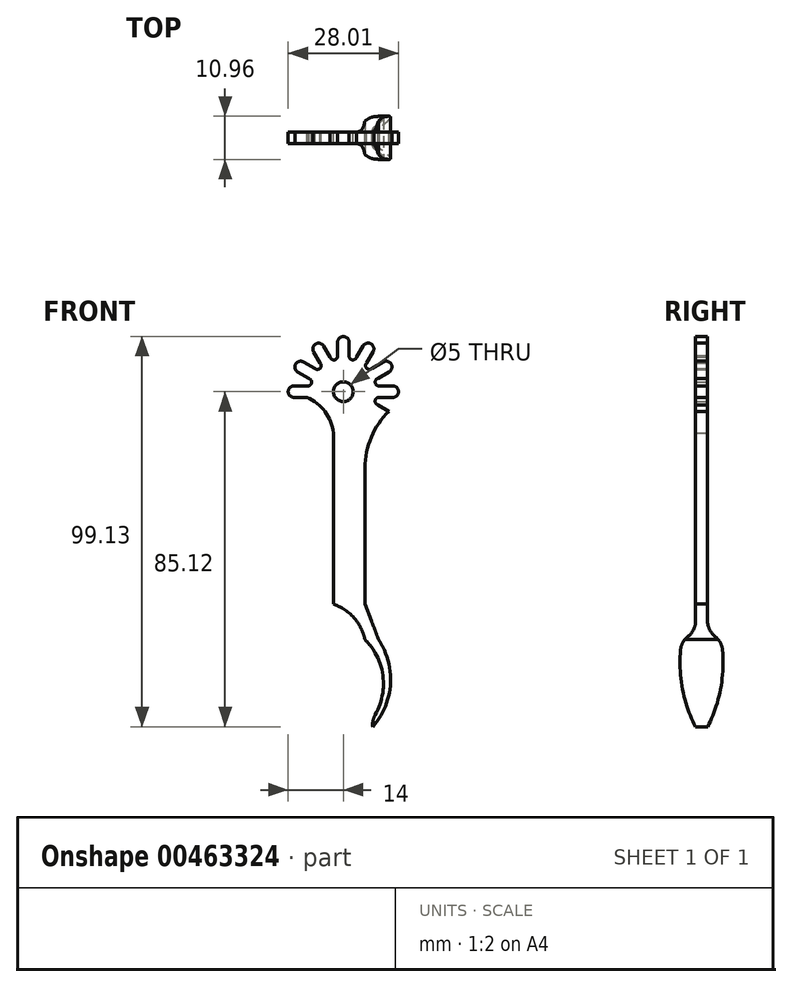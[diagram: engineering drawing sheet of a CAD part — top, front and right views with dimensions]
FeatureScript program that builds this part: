
annotation { "Feature Type Name" : "Feature", "Feature Type Description" : "" }
export const myFeature = defineFeature(function(context is Context, id is Id, definition is map)
    precondition{}
    {
        {
            var Q0;
            Q0=qCreatedBy(makeId("Front.planeOp"),FACE);
            var sketch = newSketch(context, id + "F0", { "sketchPlane" : qUnion([Q0])});
            skCircle(sketch, "E0", {"center": v(0, 0) * mm, "radius": 14 * mm, "construction": true});
            skCircle(sketch, "E1", {"center": v(0, 0) * mm, "radius": 2.5 * mm});
            skLineSegment(sketch, "E2", {"start": v(-12.53, 1.48) * mm, "end": v(-9.23, 1.48) * mm});
            skArc(sketch, "E3", {"start": v(-12.53, 1.48) * mm, "mid": v(-14, 0) * mm, "end": v(-12.53, -1.48) * mm});
            skLineSegment(sketch, "E4", {"start": v(-12.53, -1.48) * mm, "end": v(-9.23, -1.48) * mm});
            skPoint(sketch, "E5.center", {"position": v(-0.01, 0.04) * mm});
            skLineSegment(sketch, "E6.1.0", {"start": v(-11.58, 4.99) * mm, "end": v(-8.73, 3.34) * mm});
            skArc(sketch, "E6.1.1", {"start": v(-10.1, 7.54) * mm, "mid": v(-12.12, 7) * mm, "end": v(-11.58, 4.99) * mm});
            skLineSegment(sketch, "E6.1.2", {"start": v(-10.1, 7.54) * mm, "end": v(-7.26, 5.9) * mm});
            skLineSegment(sketch, "E6.2.0", {"start": v(-7.54, 10.11) * mm, "end": v(-5.9, 7.27) * mm});
            skArc(sketch, "E6.2.1", {"start": v(-4.98, 11.59) * mm, "mid": v(-7, 12.13) * mm, "end": v(-7.54, 10.11) * mm});
            skLineSegment(sketch, "E6.2.2", {"start": v(-4.98, 11.59) * mm, "end": v(-3.34, 8.74) * mm});
            skLineSegment(sketch, "E6.3.0", {"start": v(-1.47, 12.53) * mm, "end": v(-1.47, 9.24) * mm});
            skArc(sketch, "E6.3.1", {"start": v(1.48, 12.53) * mm, "mid": v(0, 14) * mm, "end": v(-1.47, 12.53) * mm});
            skLineSegment(sketch, "E6.3.2", {"start": v(1.48, 12.53) * mm, "end": v(1.48, 9.24) * mm});
            skLineSegment(sketch, "E6.4.0", {"start": v(5, 11.59) * mm, "end": v(3.35, 8.74) * mm});
            skArc(sketch, "E6.4.1", {"start": v(7.55, 10.11) * mm, "mid": v(7.01, 12.13) * mm, "end": v(5, 11.59) * mm});
            skLineSegment(sketch, "E6.4.2", {"start": v(7.55, 10.11) * mm, "end": v(5.9, 7.26) * mm});
            skLineSegment(sketch, "E6.5.0", {"start": v(10.12, 7.54) * mm, "end": v(7.27, 5.9) * mm});
            skArc(sketch, "E6.5.1", {"start": v(11.6, 4.99) * mm, "mid": v(12.14, 7) * mm, "end": v(10.12, 7.54) * mm});
            skLineSegment(sketch, "E6.5.2", {"start": v(11.6, 4.99) * mm, "end": v(8.75, 3.34) * mm});
            skLineSegment(sketch, "E6.6.0", {"start": v(12.54, 1.47) * mm, "end": v(9.25, 1.47) * mm});
            skArc(sketch, "E6.6.1", {"start": v(12.54, -1.48) * mm, "mid": v(14.01, 0) * mm, "end": v(12.54, 1.47) * mm});
            skLineSegment(sketch, "E6.6.2", {"start": v(12.54, -1.48) * mm, "end": v(9.25, -1.48) * mm});
            skLineSegment(sketch, "E6.7.0", {"start": v(11.6, -5) * mm, "end": v(8.75, -3.35) * mm});
            skLineSegment(sketch, "E6.anchor1", {"start": v(0, 0) * mm, "end": v(-12.53, -1.48) * mm, "construction": true});
            skLineSegment(sketch, "E6.anchor2", {"start": v(0, 0) * mm, "end": v(11.6, -5) * mm, "construction": true});
            skCircle(sketch, "E7", {"center": v(-0.01, 0.04) * mm, "radius": 9.33 * mm, "construction": true});
            skArc(sketch, "E8", {"start": v(-9.23, 1.47) * mm, "mid": v(-8.1, 2.17) * mm, "end": v(-8.73, 3.34) * mm});
            skArc(sketch, "E9.1.0", {"start": v(-7.26, 5.9) * mm, "mid": v(-5.92, 5.93) * mm, "end": v(-5.9, 7.27) * mm});
            skArc(sketch, "E9.2.0", {"start": v(-3.34, 8.74) * mm, "mid": v(-2.16, 8.1) * mm, "end": v(-1.47, 9.24) * mm});
            skArc(sketch, "E9.3.0", {"start": v(1.48, 9.24) * mm, "mid": v(2.18, 8.1) * mm, "end": v(3.35, 8.74) * mm});
            skArc(sketch, "E9.4.0", {"start": v(5.9, 7.26) * mm, "mid": v(5.94, 5.93) * mm, "end": v(7.27, 5.9) * mm});
            skArc(sketch, "E9.5.0", {"start": v(8.75, 3.34) * mm, "mid": v(8.1, 2.17) * mm, "end": v(9.25, 1.47) * mm});
            skArc(sketch, "E9.6.0", {"start": v(9.25, -1.48) * mm, "mid": v(8.1, -2.17) * mm, "end": v(8.75, -3.35) * mm});
            skLineSegment(sketch, "E9.anchor1", {"start": v(0, 0) * mm, "end": v(-9.24, 1.48) * mm, "construction": true});
            skLineSegment(sketch, "E9.anchor2", {"start": v(0, 0) * mm, "end": v(7.27, -5.9) * mm, "construction": true});
            skLineSegment(sketch, "E10", {"start": v(-2.48, -0.3) * mm, "end": v(-2.48, -38.57) * mm, "construction": true});
            skArc(sketch, "E11", {"start": v(-2.48, -10.54) * mm, "mid": v(-4.63, -5.1) * mm, "end": v(-9.23, -1.48) * mm});
            skLineSegment(sketch, "E12", {"start": v(-2.48, -10.54) * mm, "end": v(-2.48, -54) * mm});
            skLineSegment(sketch, "E13", {"start": v(-2.48, -54) * mm, "end": v(5.52, -54) * mm});
            skLineSegment(sketch, "E14", {"start": v(5.52, -54) * mm, "end": v(5.52, -19.35) * mm});
            skArc(sketch, "E15", {"start": v(11.6, -5) * mm, "mid": v(7.1, -11.55) * mm, "end": v(5.52, -19.35) * mm});
            skSolve(sketch);
        }
        {
            var Q0;
            Q0 = qSketchRegion(id + "F0", true);
            extrude(context, id + "F1", {"entities" : qUnion([Q0]), "endBound" : BoundingType.SYMMETRIC, "depth" : 3 * mm});
        }
        {
            var Q0;
            Q0=qCreatedBy(makeId("Front.planeOp"),FACE);
            var sketch = newSketch(context, id + "F2", { "sketchPlane" : qUnion([Q0])});
            skLineSegment(sketch, "E16.bottom", {"start": v(-9.48, -54) * mm, "end": v(12.52, -54) * mm});
            skLineSegment(sketch, "E16.top", {"start": v(-9.48, -87) * mm, "end": v(12.52, -87) * mm});
            skLineSegment(sketch, "E16.left", {"start": v(-9.48, -54) * mm, "end": v(-9.48, -87) * mm});
            skLineSegment(sketch, "E16.right", {"start": v(12.52, -54) * mm, "end": v(12.52, -87) * mm});
            skSolve(sketch);
        }
        {
            var Q0;
            Q0=makeQuery(id+"F2.imprint","IMPRINT",FACE,{"disambiguationData":[TD([[makeQuery(id+"F2.imprint","IMPRINT",EDGE,{"derivedFrom":sQuery(id+"F2.wireOp",EDGE,"E16.bottom")}),-1.0]])]});
            extrude(context, id + "F3", {"entities" : qUnion([Q0]), "operationType" : NewBodyOperationType.ADD, "endBound" : BoundingType.SYMMETRIC, "depth" : 25 * mm});
        }
        {
            var Q0;
            Q0=makeQuery(id+"F3.opExtrude","SWEPT_FACE",FACE,{"disambiguationData":[OSD([sQuery(id+"F2.wireOp",EDGE,"E16.right")])]});
            var sketch = newSketch(context, id + "F4", { "sketchPlane" : qUnion([Q0])});
            skLineSegment(sketch, "E17.bottom", {"start": v(-1.5, -54) * mm, "end": v(1.5, -54) * mm});
            skLineSegment(sketch, "E17.top", {"start": v(-1.5, -63) * mm, "end": v(1.5, -63) * mm});
            skLineSegment(sketch, "E17.left", {"start": v(-1.5, -54) * mm, "end": v(-1.5, -63) * mm});
            skLineSegment(sketch, "E17.right", {"start": v(1.5, -54) * mm, "end": v(1.5, -63) * mm});
            skLineSegment(sketch, "E18", {"start": v(5, -63) * mm, "end": v(-5, -63) * mm});
            skLineSegment(sketch, "E19", {"start": v(0, -63) * mm, "end": v(0, 139.5) * mm, "construction": true});
            skPoint(sketch, "E19.endSnap0", {"position": v(0, -87) * mm});
            skLineSegment(sketch, "E20", {"start": v(0, -87) * mm, "end": v(0, 118) * mm, "construction": true});
            skArc(sketch, "E21", {"start": v(0.54, -87) * mm, "mid": v(4.87, -75.4) * mm, "end": v(5, -63) * mm});
            skArc(sketch, "E22.MirrorCS", {"start": v(-0.54, -87) * mm, "mid": v(-4.87, -75.4) * mm, "end": v(-5, -63) * mm});
            skLineSegment(sketch, "E23", {"start": v(0.54, -87) * mm, "end": v(-0.54, -87) * mm});
            skSolve(sketch);
        }
        {
            var Q0;
            {var subQ4=sQuery(id+"F4.wireOp",EDGE,"E17.left");Q0=makeQuery(id+"F4.imprint","IMPRINT",FACE,{"disambiguationData":[TD([[makeQuery(id+"F4.imprint","IMPRINT",EDGE,{"derivedFrom":subQ4}),-1.0]])]});}
            var Q1;
            {var subQ4=sQuery(id+"F4.wireOp",EDGE,"E17.right");Q1=makeQuery(id+"F4.imprint","IMPRINT",FACE,{"disambiguationData":[TD([[makeQuery(id+"F4.imprint","IMPRINT",EDGE,{"derivedFrom":subQ4}),1.0]])]});}
            extrude(context, id + "F5", {"entities" : qUnion([Q0, Q1]), "operationType" : NewBodyOperationType.REMOVE, "oppositeDirection" : true, "depth" : 25 * mm});
        }
        {
            var Q0;
            Q0=qCreatedBy(makeId("Front.planeOp"),FACE);
            var sketch = newSketch(context, id + "F6", { "sketchPlane" : qUnion([Q0])});
            skLineSegment(sketch, "E24", {"start": v(5.52, -54) * mm, "end": v(8.93, -63) * mm});
            skLineSegment(sketch, "E25", {"start": v(8.93, -63) * mm, "end": v(19.75, -63) * mm});
            skLineSegment(sketch, "E26", {"start": v(19.75, -63) * mm, "end": v(18.1, -40.93) * mm});
            skLineSegment(sketch, "E27", {"start": v(18.1, -40.93) * mm, "end": v(5.52, -54) * mm});
            skSolve(sketch);
        }
        {
            var Q0;
            Q0 = qSketchRegion(id + "F6", true);
            extrude(context, id + "F7", {"entities" : qUnion([Q0]), "operationType" : NewBodyOperationType.REMOVE, "endBound" : BoundingType.SYMMETRIC, "depth" : 25 * mm});
        }
        {
            var Q0;
            Q0=qCreatedBy(makeId("Front.planeOp"),FACE);
            var sketch = newSketch(context, id + "F8", { "sketchPlane" : qUnion([Q0])});
            skLineSegment(sketch, "E28.bottom", {"start": v(-2.48, -54) * mm, "end": v(-15.55, -54) * mm});
            skLineSegment(sketch, "E28.top", {"start": v(-2.48, -90.5) * mm, "end": v(-15.55, -90.5) * mm});
            skLineSegment(sketch, "E28.left", {"start": v(-2.48, -54) * mm, "end": v(-2.48, -90.5) * mm});
            skLineSegment(sketch, "E28.right", {"start": v(-15.55, -54) * mm, "end": v(-15.55, -90.5) * mm});
            skSolve(sketch);
        }
        {
            var Q0;
            Q0=makeQuery(id+"F8.imprint","IMPRINT",FACE,{"disambiguationData":[TD([[makeQuery(id+"F8.imprint","IMPRINT",EDGE,{"derivedFrom":sQuery(id+"F8.wireOp",EDGE,"E28.bottom")}),1.0]])]});
            extrude(context, id + "F9", {"entities" : qUnion([Q0]), "operationType" : NewBodyOperationType.REMOVE, "endBound" : BoundingType.SYMMETRIC, "depth" : 25 * mm});
        }
        {
            var Q0;
            Q0=qCreatedBy(makeId("Front.planeOp"),FACE);
            var sketch = newSketch(context, id + "F10", { "sketchPlane" : qUnion([Q0])});
            skArc(sketch, "E29", {"start": v(7.47, -85.12) * mm, "mid": v(11.95, -74.3) * mm, "end": v(8.93, -63) * mm});
            skArc(sketch, "E30", {"start": v(5.84, -85.12) * mm, "mid": v(10.19, -73.99) * mm, "end": v(5.49, -63) * mm});
            skLineSegment(sketch, "E31", {"start": v(7.47, -85.12) * mm, "end": v(5.84, -85.12) * mm});
            skArc(sketch, "E32", {"start": v(5.49, -63) * mm, "mid": v(2.7, -57.44) * mm, "end": v(-2.48, -54) * mm});
            skLineSegment(sketch, "E33", {"start": v(5.52, -54) * mm, "end": v(-4.73, -54) * mm, "construction": true});
            skLineSegment(sketch, "E34", {"start": v(-4.73, -54) * mm, "end": v(-25.9, -62.6) * mm});
            skLineSegment(sketch, "E35", {"start": v(-25.9, -62.6) * mm, "end": v(-15.06, -81.79) * mm});
            skLineSegment(sketch, "E36", {"start": v(-15.06, -81.79) * mm, "end": v(-7.87, -94.52) * mm});
            skLineSegment(sketch, "E37", {"start": v(-7.87, -94.52) * mm, "end": v(22.75, -94.52) * mm});
            skLineSegment(sketch, "E38", {"start": v(22.75, -94.52) * mm, "end": v(21.3, -60.68) * mm});
            skLineSegment(sketch, "E39", {"start": v(21.3, -60.68) * mm, "end": v(12.96, -58.57) * mm});
            skLineSegment(sketch, "E40", {"start": v(12.96, -58.57) * mm, "end": v(8.93, -63) * mm});
            skLineSegment(sketch, "E41", {"start": v(-2.48, -54) * mm, "end": v(-4.73, -54) * mm});
            skSolve(sketch);
        }
        {
            var Q0;
            Q0=makeQuery(id+"F10.imprint","IMPRINT",FACE,{"disambiguationData":[TD([[makeQuery(id+"F10.imprint","IMPRINT",EDGE,{"derivedFrom":sQuery(id+"F10.wireOp",EDGE,"E29")}),-1.0]])]});
            extrude(context, id + "F11", {"entities" : qUnion([Q0]), "operationType" : NewBodyOperationType.REMOVE, "endBound" : BoundingType.SYMMETRIC, "oppositeDirection" : true, "depth" : 25 * mm});
        }
        {
            var Q0;
            Q0=makeQuery(id+"F5.boolean.opBoolean","COPY",EDGE,{"derivedFrom":makeQuery(id+"F5.opExtrude","SWEPT_EDGE",EDGE,{"disambiguationData":[OSD([sQuery(id+"F4.wireOp",EDGE,"E17.left"),sQuery(id+"F4.wireOp",EDGE,"E18")])]})});
            var Q1;
            Q1=makeQuery(id+"F5.boolean.opBoolean","COPY",EDGE,{"derivedFrom":makeQuery(id+"F5.opExtrude","SWEPT_EDGE",EDGE,{"disambiguationData":[OSD([sQuery(id+"F4.wireOp",EDGE,"E17.right"),sQuery(id+"F4.wireOp",EDGE,"E18")])]})});
            fillet(context, id + "F12", {"entities" : qUnion([Q0, Q1]), "radius" : 5 * mm, "tangentPropagation" : true, "allowEdgeOverflow" : false});
        }
        {
            var Q0;
            Q0=makeQuery(id+"F11.boolean.opBoolean","COPY",EDGE,{"derivedFrom":makeQuery(id+"F11.opExtrude","SWEPT_EDGE",EDGE,{"disambiguationData":[OSD([sQuery(id+"F10.wireOp",EDGE,"E32"),sQuery(id+"F10.wireOp",EDGE,"E41")])]})});
            var Q1;
            Q1=makeQuery(id+"F12.opFillet","BLEND_EDGE",EDGE,{"blendedFrom":[makeQuery(id+"F5.boolean.opBoolean","COPY",EDGE,{"derivedFrom":makeQuery(id+"F5.opExtrude","SWEPT_EDGE",EDGE,{"disambiguationData":[OSD([sQuery(id+"F4.wireOp",EDGE,"E17.left"),sQuery(id+"F4.wireOp",EDGE,"E18")])]})}),makeQuery(id+"F5.boolean.opBoolean","COPY",FACE,{"derivedFrom":makeQuery(id+"F5.opExtrude","SWEPT_FACE",FACE,{"disambiguationData":[OSD([sQuery(id+"F4.wireOp",EDGE,"E22.MirrorCS")])]})})],"blendedInto":[makeQuery(id+"F5.boolean.opBoolean","COPY",FACE,{"derivedFrom":makeQuery(id+"F5.opExtrude","SWEPT_FACE",FACE,{"disambiguationData":[OSD([sQuery(id+"F4.wireOp",EDGE,"E22.MirrorCS")])]})})]});
            var Q2;
            Q2=makeQuery(id+"F12.opFillet","BLEND_EDGE",EDGE,{"blendedFrom":[makeQuery(id+"F5.boolean.opBoolean","COPY",EDGE,{"derivedFrom":makeQuery(id+"F5.opExtrude","SWEPT_EDGE",EDGE,{"disambiguationData":[OSD([sQuery(id+"F4.wireOp",EDGE,"E17.right"),sQuery(id+"F4.wireOp",EDGE,"E18")])]})}),makeQuery(id+"F5.boolean.opBoolean","COPY",FACE,{"derivedFrom":makeQuery(id+"F5.opExtrude","SWEPT_FACE",FACE,{"disambiguationData":[OSD([sQuery(id+"F4.wireOp",EDGE,"E21")])]})})],"blendedInto":[makeQuery(id+"F5.boolean.opBoolean","COPY",FACE,{"derivedFrom":makeQuery(id+"F5.opExtrude","SWEPT_FACE",FACE,{"disambiguationData":[OSD([sQuery(id+"F4.wireOp",EDGE,"E21")])]})})]});
            var Q3;
            Q3=makeQuery(id+"F11.boolean.opBoolean","COPY",EDGE,{"derivedFrom":makeQuery(id+"F11.opExtrude","SWEPT_EDGE",EDGE,{"disambiguationData":[OSD([sQuery(id+"F10.wireOp",EDGE,"E30"),sQuery(id+"F10.wireOp",EDGE,"E31")])]})});
            fillet(context, id + "F13", {"entities" : qUnion([Q0, Q1, Q2, Q3]), "radius" : 5 * mm, "tangentPropagation" : true, "allowEdgeOverflow" : false});
        }
    });
